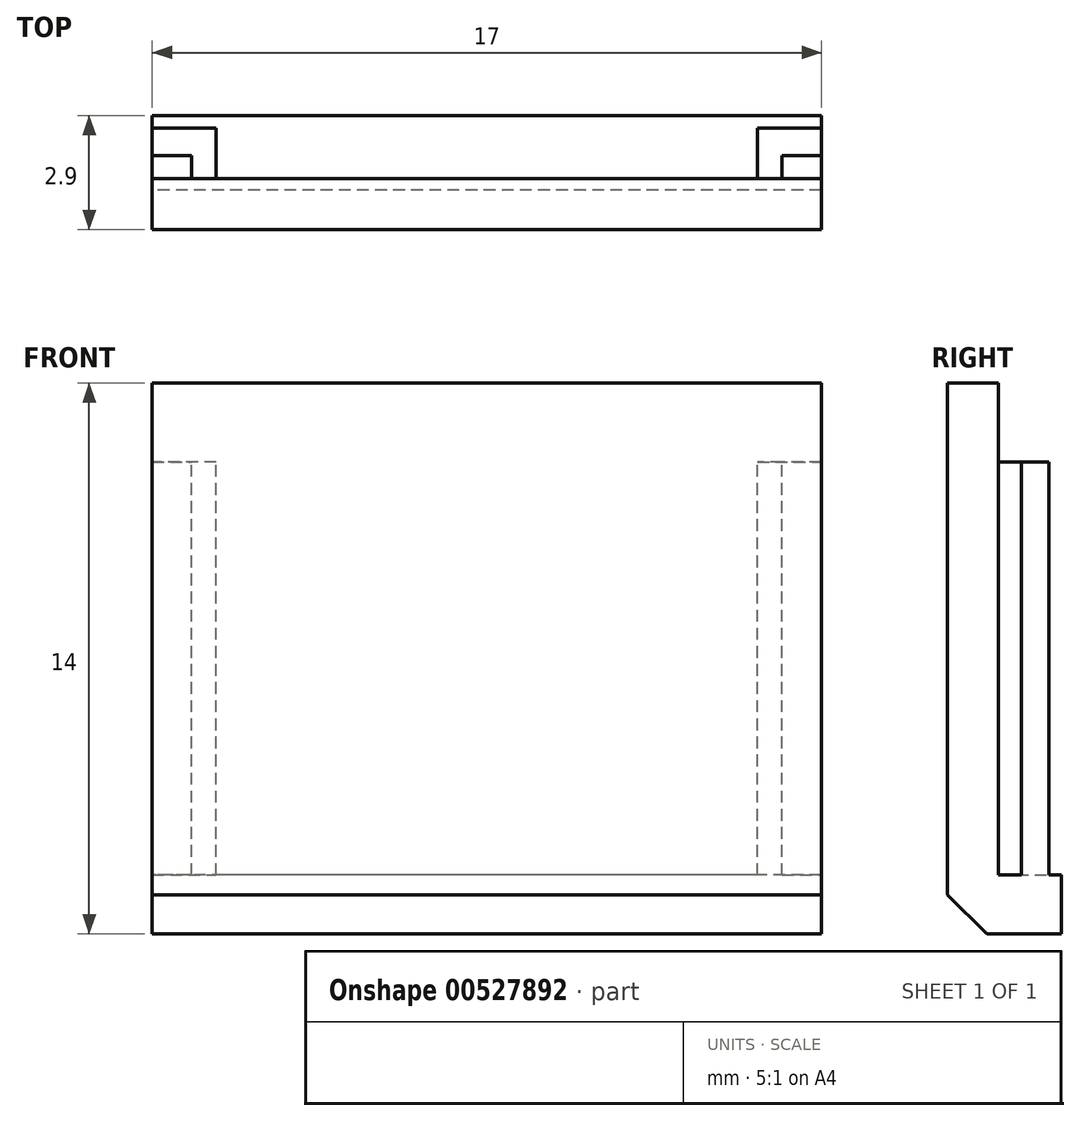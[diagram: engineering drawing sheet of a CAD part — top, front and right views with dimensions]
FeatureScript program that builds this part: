
annotation { "Feature Type Name" : "Feature", "Feature Type Description" : "" }
export const myFeature = defineFeature(function(context is Context, id is Id, definition is map)
    precondition{}
    {
        {
            var Q0;
            Q0=qCreatedBy(makeId("Top.planeOp"),FACE);
            var sketch = newSketch(context, id + "F0", { "sketchPlane" : qUnion([Q0])});
            skLineSegment(sketch, "E0", {"start": v(0, 0) * mm, "end": v(17, 0) * mm});
            skLineSegment(sketch, "E1", {"start": v(17, 0) * mm, "end": v(17, 2.9) * mm});
            skLineSegment(sketch, "E2", {"start": v(17, 2.9) * mm, "end": v(0, 2.9) * mm});
            skLineSegment(sketch, "E3", {"start": v(0, 2.9) * mm, "end": v(0, 0) * mm});
            skSolve(sketch);
        }
        {
            var Q0;
            Q0=qSketchRegion(id+"F0",true);
            extrude(context, id + "F1", {"entities" : qUnion([Q0]), "depth" : 14 * mm});
        }
        {
            var Q0;
            Q0=makeQuery(id+"F1.opExtrude","CAP_FACE",FACE,{"disambiguationData":[OSD([sQuery(id+"F0.wireOp",EDGE,"E0"),sQuery(id+"F0.wireOp",EDGE,"E1"),sQuery(id+"F0.wireOp",EDGE,"E2"),sQuery(id+"F0.wireOp",EDGE,"E3")])],"isStart":false});
            var sketch = newSketch(context, id + "F2", { "sketchPlane" : qUnion([Q0])});
            skLineSegment(sketch, "E4", {"start": v(8.5, 2.9) * mm, "end": v(15.38, 2.9) * mm});
            skLineSegment(sketch, "E5", {"start": v(15.38, 2.9) * mm, "end": v(15.38, 1.3) * mm});
            skLineSegment(sketch, "E6", {"start": v(15.38, 1.3) * mm, "end": v(1.63, 1.3) * mm});
            skLineSegment(sketch, "E7", {"start": v(1.63, 1.3) * mm, "end": v(1.63, 2.9) * mm});
            skLineSegment(sketch, "E8", {"start": v(1.63, 2.9) * mm, "end": v(8.5, 2.9) * mm});
            skLineSegment(sketch, "E9", {"start": v(17, 0) * mm, "end": v(17, 1.3) * mm, "construction": true});
            skLineSegment(sketch, "E10", {"start": v(17, 1.3) * mm, "end": v(16, 1.3) * mm});
            skLineSegment(sketch, "E11", {"start": v(16, 1.3) * mm, "end": v(16, 1.88) * mm});
            skLineSegment(sketch, "E12", {"start": v(16, 1.88) * mm, "end": v(17, 1.88) * mm});
            skLineSegment(sketch, "E13", {"start": v(17, 1.88) * mm, "end": v(17, 1.3) * mm});
            skLineSegment(sketch, "E14", {"start": v(17, 1.88) * mm, "end": v(17, 2.58) * mm, "construction": true});
            skLineSegment(sketch, "E15", {"start": v(17, 2.58) * mm, "end": v(15.38, 2.58) * mm});
            skLineSegment(sketch, "E16", {"start": v(15.38, 2.9) * mm, "end": v(17, 2.9) * mm});
            skLineSegment(sketch, "E17", {"start": v(17, 2.9) * mm, "end": v(17, 2.58) * mm});
            skLineSegment(sketch, "E18", {"start": v(8.5, 2.9) * mm, "end": v(8.5, 0) * mm, "construction": true});
            skLineSegment(sketch, "E19.MirrorCS", {"start": v(0, 1.3) * mm, "end": v(1, 1.3) * mm});
            skLineSegment(sketch, "E20.MirrorCS", {"start": v(0, 1.88) * mm, "end": v(0, 1.3) * mm});
            skLineSegment(sketch, "E21.MirrorCS", {"start": v(1, 1.88) * mm, "end": v(0, 1.88) * mm});
            skLineSegment(sketch, "E22.MirrorCS", {"start": v(1, 1.3) * mm, "end": v(1, 1.88) * mm});
            skLineSegment(sketch, "E23.MirrorCS", {"start": v(1.63, 2.9) * mm, "end": v(0, 2.9) * mm});
            skLineSegment(sketch, "E24.MirrorCS", {"start": v(0, 2.58) * mm, "end": v(1.62, 2.58) * mm});
            skLineSegment(sketch, "E25.MirrorCS", {"start": v(0, 2.9) * mm, "end": v(0, 2.58) * mm});
            skSolve(sketch);
        }
        {
            var Q0;
            Q0=qSketchRegion(id+"F2",true);
            extrude(context, id + "F3", {"entities" : qUnion([Q0]), "operationType" : NewBodyOperationType.REMOVE, "oppositeDirection" : true, "depth" : 12.5 * mm});
        }
        {
            var Q0;
            Q0=makeQuery(id+"F1.opExtrude","CAP_FACE",FACE,{"disambiguationData":[OSD([sQuery(id+"F0.wireOp",EDGE,"E0"),sQuery(id+"F0.wireOp",EDGE,"E1"),sQuery(id+"F0.wireOp",EDGE,"E2"),sQuery(id+"F0.wireOp",EDGE,"E3")])],"isStart":false});
            var sketch = newSketch(context, id + "F4", { "sketchPlane" : qUnion([Q0])});
            skLineSegment(sketch, "E26", {"start": v(0, 1.3) * mm, "end": v(17, 1.3) * mm});
            skLineSegment(sketch, "E27.0", {"start": v(17, 2.9) * mm, "end": v(0, 2.9) * mm});
            skLineSegment(sketch, "E28", {"start": v(17, 1.3) * mm, "end": v(17, 2.9) * mm});
            skLineSegment(sketch, "E29", {"start": v(0, 2.9) * mm, "end": v(0, 1.3) * mm});
            skSolve(sketch);
        }
        {
            var Q0;
            Q0=qSketchRegion(id+"F4",true);
            extrude(context, id + "F5", {"entities" : qUnion([Q0]), "operationType" : NewBodyOperationType.REMOVE, "oppositeDirection" : true, "depth" : 2 * mm});
        }
        {
            var Q0;
            Q0=makeQuery(id+"F1.opExtrude","CAP_EDGE",EDGE,{"disambiguationData":[OSD([sQuery(id+"F0.wireOp",EDGE,"E0")])],"isStart":true});
            chamfer(context, id + "F6", {"entities" : qUnion([Q0]), "width" : 1 * mm, "tangentPropagation" : true});
        }
    });
